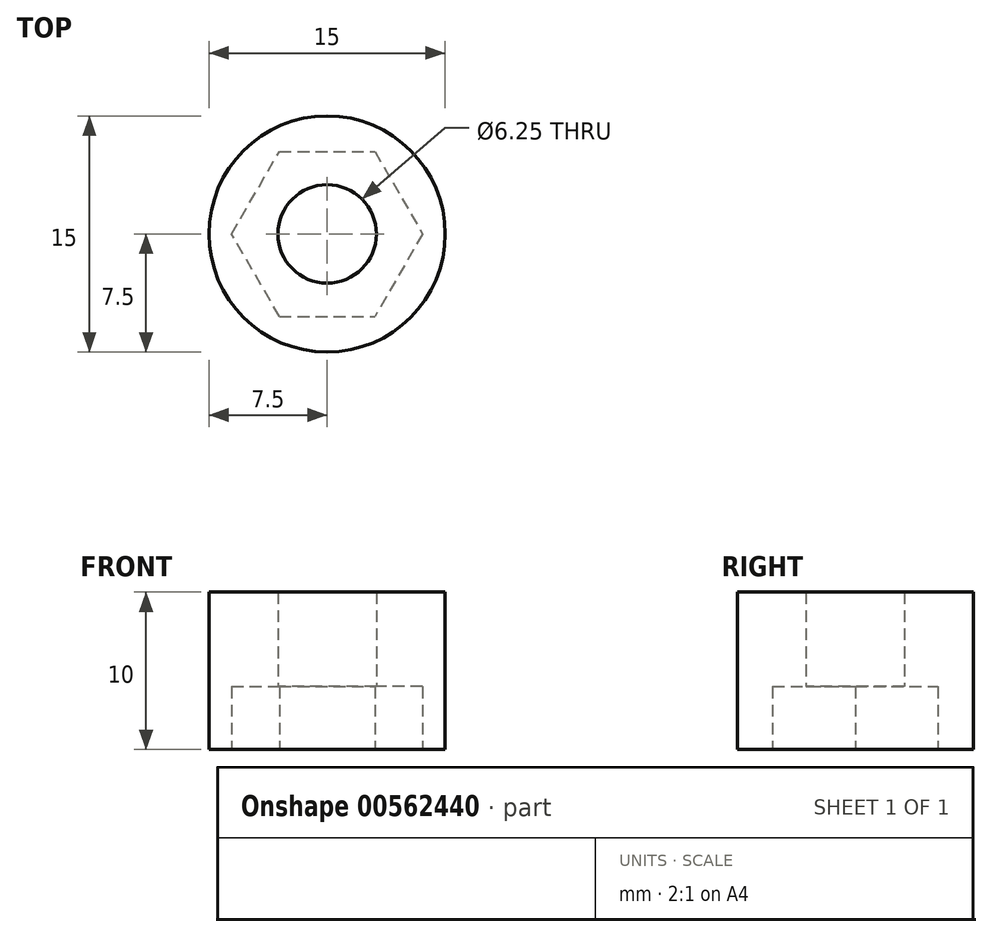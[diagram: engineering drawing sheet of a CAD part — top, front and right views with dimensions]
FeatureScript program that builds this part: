
annotation { "Feature Type Name" : "Feature", "Feature Type Description" : "" }
export const myFeature = defineFeature(function(context is Context, id is Id, definition is map)
    precondition{}
    {
        {
            var Q0;
            Q0=qCreatedBy(makeId("Top.planeOp"),FACE);
            var sketch = newSketch(context, id + "F0", { "sketchPlane" : qUnion([Q0])});
            skCircle(sketch, "E0", {"center": v(0, 0) * mm, "radius": 3.12 * mm});
            skCircle(sketch, "E1.cCircle", {"center": v(0, 0) * mm, "radius": 5.25 * mm, "construction": true});
            skLineSegment(sketch, "E1.0", {"start": v(6.06, 0) * mm, "end": v(3.03, -5.25) * mm});
            skLineSegment(sketch, "E1.2", {"start": v(-3.03, -5.25) * mm, "end": v(-6.06, 0) * mm});
            skLineSegment(sketch, "E1.3", {"start": v(-6.06, 0) * mm, "end": v(-3.03, 5.25) * mm});
            skLineSegment(sketch, "E1.4", {"start": v(-3.03, 5.25) * mm, "end": v(3.03, 5.25) * mm});
            skLineSegment(sketch, "E1.5", {"start": v(3.03, 5.25) * mm, "end": v(6.06, 0) * mm});
            skLineSegment(sketch, "E2", {"start": v(-3.03, -5.25) * mm, "end": v(3.03, -5.25) * mm});
            skCircle(sketch, "E3", {"center": v(0, 0) * mm, "radius": 7.5 * mm});
            skLineSegment(sketch, "E4", {"start": v(0, 0) * mm, "end": v(6.5, 3.75) * mm, "construction": true});
            skCircle(sketch, "E5.cCircle", {"center": v(29.93, 2.76) * mm, "radius": 5.25 * mm, "construction": true});
            skLineSegment(sketch, "E5.0", {"start": v(36, 2.76) * mm, "end": v(32.96, -2.5) * mm});
            skLineSegment(sketch, "E5.2", {"start": v(26.9, -2.5) * mm, "end": v(23.87, 2.76) * mm});
            skLineSegment(sketch, "E5.3", {"start": v(23.87, 2.76) * mm, "end": v(26.9, 8) * mm});
            skLineSegment(sketch, "E5.4", {"start": v(26.9, 8) * mm, "end": v(32.96, 8) * mm});
            skLineSegment(sketch, "E5.5", {"start": v(32.96, 8) * mm, "end": v(36, 2.76) * mm});
            skLineSegment(sketch, "E6", {"start": v(26.9, -2.5) * mm, "end": v(32.96, -2.5) * mm});
            skLineSegment(sketch, "E7", {"start": v(29.93, 2.76) * mm, "end": v(34.48, 5.38) * mm, "construction": true});
            skCircle(sketch, "E8", {"center": v(29.93, 2.76) * mm, "radius": 7.5 * mm});
            skCircle(sketch, "E9", {"center": v(29.93, 2.76) * mm, "radius": 3.12 * mm});
            skSolve(sketch);
        }
        {
            var Q0;
            Q0=makeQuery(id+"F0.imprint","IMPRINT",FACE,{"disambiguationData":[TD([[makeQuery(id+"F0.imprint","IMPRINT",EDGE,{"derivedFrom":sQuery(id+"F0.wireOp",EDGE,"E1.0")}),1.0]])]});
            var Q1;
            Q1=makeQuery(id+"F0.imprint","IMPRINT",FACE,{"disambiguationData":[TD([[makeQuery(id+"F0.imprint","IMPRINT",EDGE,{"derivedFrom":sQuery(id+"F0.wireOp",EDGE,"E0")}),-1.0]])]});
            extrude(context, id + "F1", {"entities" : qUnion([Q0, Q1]), "depth" : 10 * mm, "offsetDistance" : 25 * mm});
        }
        {
            var Q0;
            Q0=makeQuery(id+"F0.imprint","IMPRINT",FACE,{"disambiguationData":[TD([[makeQuery(id+"F0.imprint","IMPRINT",EDGE,{"derivedFrom":sQuery(id+"F0.wireOp",EDGE,"E0")}),-1.0]])]});
            extrude(context, id + "F2", {"entities" : qUnion([Q0]), "operationType" : NewBodyOperationType.REMOVE, "depth" : 4 * mm, "offsetDistance" : 25 * mm});
        }
    });
